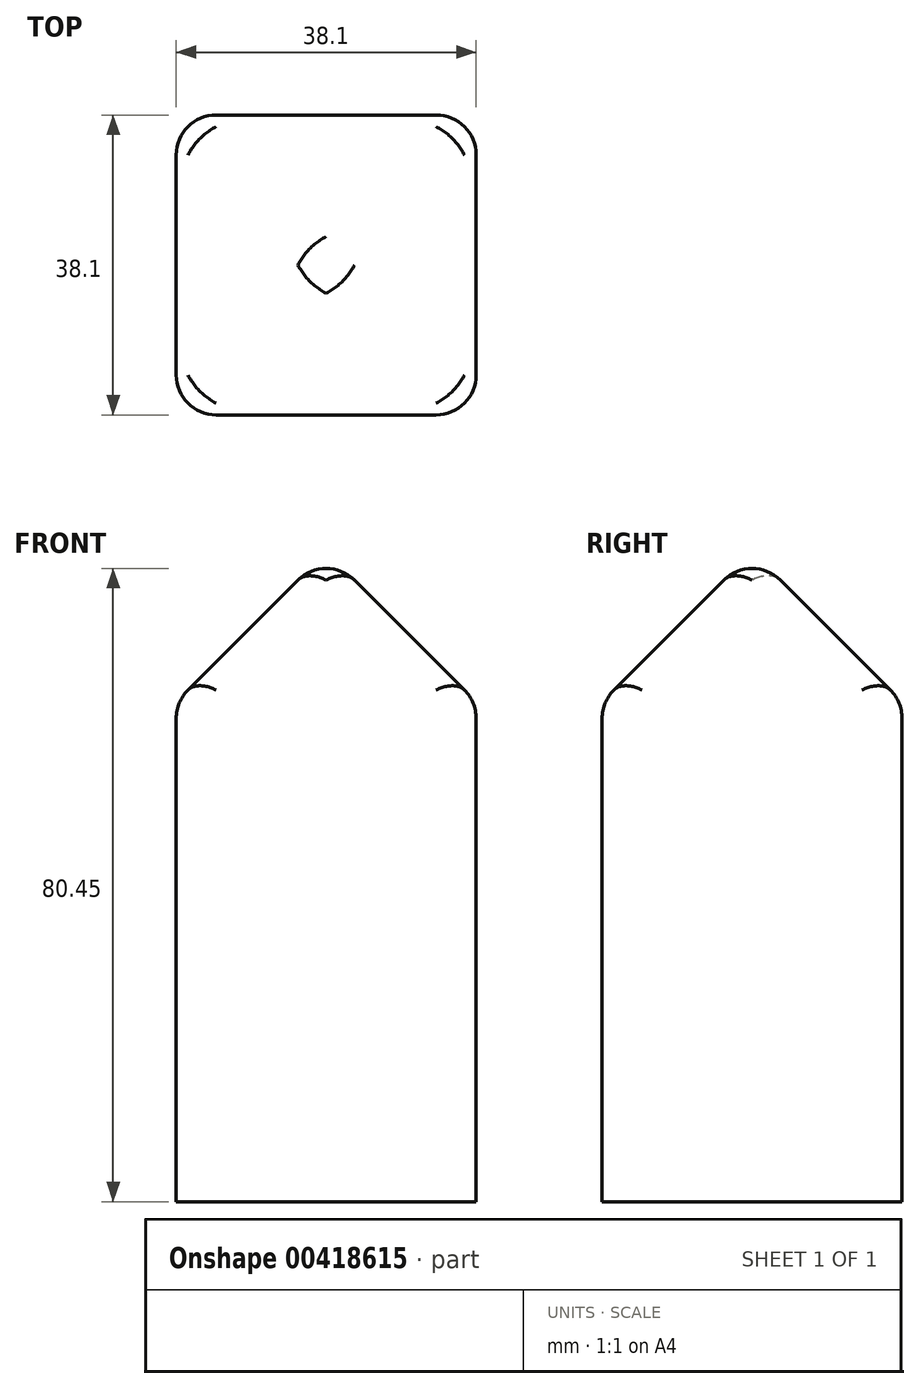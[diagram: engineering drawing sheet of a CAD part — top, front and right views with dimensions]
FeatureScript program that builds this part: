
annotation { "Feature Type Name" : "Feature", "Feature Type Description" : "" }
export const myFeature = defineFeature(function(context is Context, id is Id, definition is map)
    precondition{}
    {
        {
            var Q0;
            Q0=qCreatedBy(makeId("Top.planeOp"),FACE);
            var sketch = newSketch(context, id + "F0", { "sketchPlane" : qUnion([Q0])});
            skLineSegment(sketch, "E0.bottom", {"start": v(19.05, -19.05) * mm, "end": v(-19.05, -19.05) * mm});
            skLineSegment(sketch, "E0.top", {"start": v(19.05, 19.05) * mm, "end": v(-19.05, 19.05) * mm});
            skLineSegment(sketch, "E0.left", {"start": v(19.05, -19.05) * mm, "end": v(19.05, 19.05) * mm});
            skLineSegment(sketch, "E0.right", {"start": v(-19.05, -19.05) * mm, "end": v(-19.05, 19.05) * mm});
            skPoint(sketch, "E0.middle", {"position": v(0, 0) * mm});
            skSolve(sketch);
        }
        {
            var Q0;
            Q0=makeQuery(id+"F0.imprint","IMPRINT",FACE,{"disambiguationData":[TD([[makeQuery(id+"F0.imprint","IMPRINT",EDGE,{"derivedFrom":sQuery(id+"F0.wireOp",EDGE,"E0.bottom")}),-1.0]])]});
            var sketch = newSketch(context, id + "F1", { "sketchPlane" : qUnion([Q0])});
            skSolve(sketch);
        }
        {
            var Q0;
            Q0=makeQuery(id+"F1.imprint","IMPRINT",FACE,{"disambiguationData":[TD([[makeQuery(id+"F1.imprint","IMPRINT",EDGE,{"derivedFrom":makeQuery(id+"F0.imprint","IMPRINT",EDGE,{"derivedFrom":sQuery(id+"F0.wireOp",EDGE,"E0.bottom")})}),-1.0]])]});
            extrude(context, id + "F2", {"entities" : qUnion([Q0]), "endBound" : BoundingType.SYMMETRIC, "depth" : 63.5 * mm});
        }
        {
            var Q0;
            Q0=makeQuery(id+"F2.opExtrude","CAP_FACE",FACE,{"disambiguationData":[OSD([sQuery(id+"F0.wireOp",EDGE,"E0.bottom"),sQuery(id+"F0.wireOp",EDGE,"E0.top"),sQuery(id+"F0.wireOp",EDGE,"E0.left"),sQuery(id+"F0.wireOp",EDGE,"E0.right")])],"isStart":false});
            var sketch = newSketch(context, id + "F3", { "sketchPlane" : qUnion([Q0])});
            skLineSegment(sketch, "E1", {"start": v(19.05, 19.05) * mm, "end": v(0, 0) * mm});
            skLineSegment(sketch, "E2", {"start": v(0, 0) * mm, "end": v(-19.05, 19.05) * mm});
            skLineSegment(sketch, "E3", {"start": v(-19.05, 19.05) * mm, "end": v(0, 0) * mm});
            skLineSegment(sketch, "E4", {"start": v(0, 0) * mm, "end": v(-19.05, -19.05) * mm});
            skLineSegment(sketch, "E5", {"start": v(0, 0) * mm, "end": v(19.05, -19.05) * mm});
            skLineSegment(sketch, "E6", {"start": v(19.05, -19.05) * mm, "end": v(-19.05, 19.05) * mm});
            skLineSegment(sketch, "E7", {"start": v(-19.05, 19.05) * mm, "end": v(19.05, 19.05) * mm});
            skLineSegment(sketch, "E8", {"start": v(19.05, 19.05) * mm, "end": v(19.05, -19.05) * mm});
            skLineSegment(sketch, "E9", {"start": v(19.05, -19.05) * mm, "end": v(-19.05, -19.05) * mm});
            skLineSegment(sketch, "E10", {"start": v(-19.05, -19.05) * mm, "end": v(-19.05, 19.05) * mm});
            skSolve(sketch);
        }
        {
            var Q0;
            {var subQ0=sQuery(id+"F3.wireOp",EDGE,"E1");Q0=makeQuery(id+"F3.imprint","IMPRINT",FACE,{"disambiguationData":[TD([[makeQuery(id+"F3.imprint","IMPRINT",EDGE,{"derivedFrom":subQ0}),1.0]])]});}
            extrude(context, id + "F4", {"entities" : qUnion([Q0]), "operationType" : NewBodyOperationType.ADD, "depth" : 19.05 * mm});
        }
        {
            var Q0;
            Q0=makeQuery(id+"F4.opExtrude","CAP_EDGE",EDGE,{"disambiguationData":[OSD([sQuery(id+"F3.wireOp",EDGE,"E8")])],"isStart":false});
            chamfer(context, id + "F5", {"entities" : qUnion([Q0]), "width" : 19.05 * mm, "tangentPropagation" : true});
        }
        {
            var Q0;
            {var subQ0=sQuery(id+"F3.wireOp",EDGE,"E4");Q0=makeQuery(id+"F3.imprint","IMPRINT",FACE,{"disambiguationData":[TD([[makeQuery(id+"F3.imprint","IMPRINT",EDGE,{"derivedFrom":subQ0}),1.0]])]});}
            var Q1;
            {var subQ0=sQuery(id+"F3.wireOp",EDGE,"E4");Q1=makeQuery(id+"F3.imprint","IMPRINT",FACE,{"disambiguationData":[TD([[makeQuery(id+"F3.imprint","IMPRINT",EDGE,{"derivedFrom":subQ0}),-1.0]])]});}
            var Q2;
            {var subQ0=sQuery(id+"F3.wireOp",EDGE,"E1");Q2=makeQuery(id+"F3.imprint","IMPRINT",FACE,{"disambiguationData":[TD([[makeQuery(id+"F3.imprint","IMPRINT",EDGE,{"derivedFrom":subQ0}),-1.0]])]});}
            extrude(context, id + "F6", {"entities" : qUnion([Q0, Q1, Q2]), "operationType" : NewBodyOperationType.ADD, "depth" : 19.05 * mm});
        }
        {
            var Q0;
            Q0=makeQuery(id+"F6.opExtrude","CAP_EDGE",EDGE,{"disambiguationData":[OSD([sQuery(id+"F3.wireOp",EDGE,"E7")])],"isStart":false});
            var Q1;
            Q1=makeQuery(id+"F6.opExtrude","CAP_EDGE",EDGE,{"disambiguationData":[OSD([sQuery(id+"F3.wireOp",EDGE,"E10")])],"isStart":false});
            var Q2;
            Q2=makeQuery(id+"F6.opExtrude","CAP_EDGE",EDGE,{"disambiguationData":[OSD([sQuery(id+"F3.wireOp",EDGE,"E9")])],"isStart":false});
            chamfer(context, id + "F7", {"entities" : qUnion([Q0, Q1, Q2]), "chamferType" : ChamferType.OFFSET_ANGLE, "width" : 19.05 * mm, "oppositeDirection" : false, "angle" : 45 * degree, "tangentPropagation" : true});
        }
        {
            var Q0;
            Q0=makeQuery(id+"F7.opChamfer","BLEND_FACE",FACE,{"disambiguationData":[OSD([sQuery(id+"F3.wireOp",EDGE,"E10")])]});
            var Q1;
            Q1=makeQuery(id+"F5.opChamfer","BLEND_FACE",FACE,{"disambiguationData":[OSD([sQuery(id+"F3.wireOp",EDGE,"E8")])]});
            fillet(context, id + "F8", {"entities" : qUnion([Q0, Q1]), "radius" : 5.08 * mm, "tangentPropagation" : true, "allowEdgeOverflow" : false});
        }
        {
            var Q0;
            Q0=makeQuery(id+"F6.boolean.opBoolean","MERGE",EDGE,{"derivedFrom":[makeQuery(id+"F2.opExtrude","SWEPT_EDGE",EDGE,{"disambiguationData":[OSD([sQuery(id+"F0.wireOp",EDGE,"E0.top"),sQuery(id+"F0.wireOp",EDGE,"E0.right")])]}),makeQuery(id+"F6.opExtrude","SWEPT_EDGE",EDGE,{"disambiguationData":[OSD([sQuery(id+"F3.wireOp",EDGE,"E6"),sQuery(id+"F3.wireOp",EDGE,"E7"),sQuery(id+"F3.wireOp",EDGE,"E10")])]})]});
            var Q1;
            Q1=makeQuery(id+"F2.opExtrude","SWEPT_EDGE",EDGE,{"disambiguationData":[OSD([sQuery(id+"F0.wireOp",EDGE,"E0.top"),sQuery(id+"F0.wireOp",EDGE,"E0.left")])]});
            var Q2;
            {var subQ0=sQuery(id+"F3.wireOp",EDGE,"E7");Q2=makeQuery(id+"F7.opChamfer","BLEND_EDGE",EDGE,{"blendedFrom":[makeQuery(id+"F6.opExtrude","CAP_EDGE",EDGE,{"disambiguationData":[OSD([subQ0])],"isStart":false}),makeQuery(id+"F6.boolean.opBoolean","MERGE",FACE,{"derivedFrom":[makeQuery(id+"F2.opExtrude","SWEPT_FACE",FACE,{"disambiguationData":[OSD([sQuery(id+"F0.wireOp",EDGE,"E0.top")])]}),makeQuery(id+"F6.opExtrude","SWEPT_FACE",FACE,{"disambiguationData":[OSD([subQ0])]})]})],"blendedInto":[makeQuery(id+"F6.boolean.opBoolean","MERGE",FACE,{"derivedFrom":[makeQuery(id+"F2.opExtrude","SWEPT_FACE",FACE,{"disambiguationData":[OSD([sQuery(id+"F0.wireOp",EDGE,"E0.top")])]}),makeQuery(id+"F6.opExtrude","SWEPT_FACE",FACE,{"disambiguationData":[OSD([subQ0])]})]})]});}
            var Q3;
            Q3=makeQuery(id+"F2.opExtrude","SWEPT_EDGE",EDGE,{"disambiguationData":[OSD([sQuery(id+"F0.wireOp",EDGE,"E0.bottom"),sQuery(id+"F0.wireOp",EDGE,"E0.left")])]});
            var Q4;
            Q4=makeQuery(id+"F6.boolean.opBoolean","MERGE",EDGE,{"derivedFrom":[makeQuery(id+"F2.opExtrude","SWEPT_EDGE",EDGE,{"disambiguationData":[OSD([sQuery(id+"F0.wireOp",EDGE,"E0.bottom"),sQuery(id+"F0.wireOp",EDGE,"E0.right")])]}),makeQuery(id+"F6.opExtrude","SWEPT_EDGE",EDGE,{"disambiguationData":[OSD([sQuery(id+"F3.wireOp",EDGE,"E4"),sQuery(id+"F3.wireOp",EDGE,"E9"),sQuery(id+"F3.wireOp",EDGE,"E10")])]})]});
            fillet(context, id + "F9", {"entities" : qUnion([Q0, Q1, Q2, Q3, Q4]), "radius" : 5.08 * mm, "tangentPropagation" : true, "allowEdgeOverflow" : false});
        }
    });
